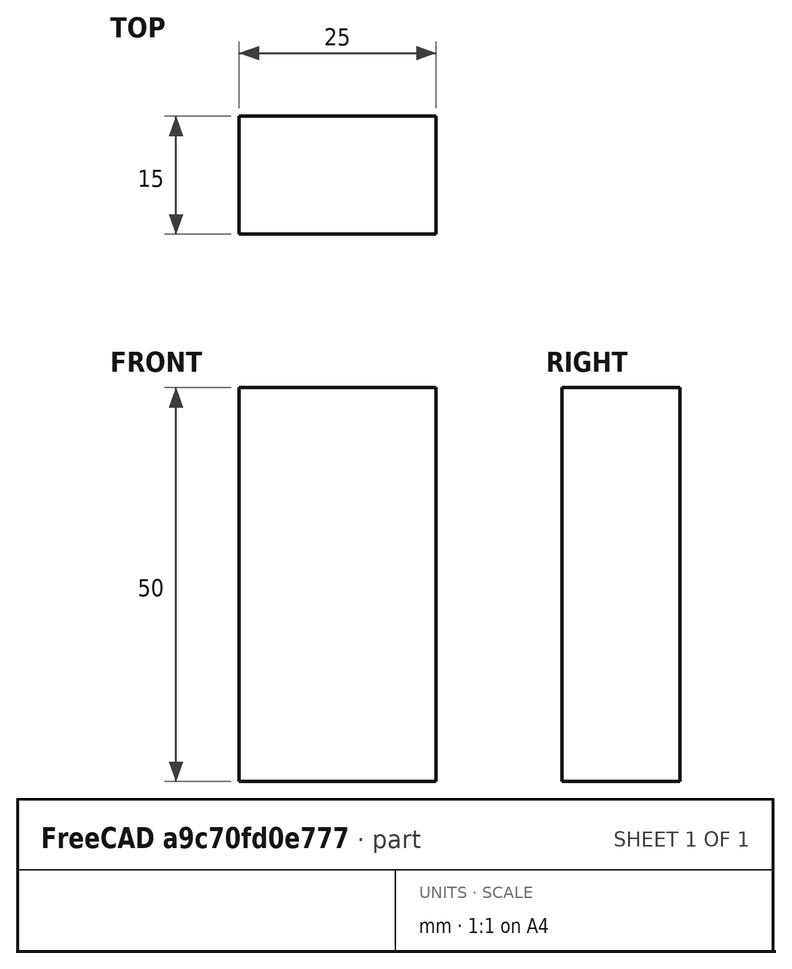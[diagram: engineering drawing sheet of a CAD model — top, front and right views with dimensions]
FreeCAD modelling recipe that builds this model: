
FCSTD DOCUMENT  (FreeCAD 0.15R4671 (Git))
Label: Flat Bar 25x15 EN10058 S235JR
License: All rights reserved
LicenseURL: http://en.wikipedia.org/wiki/All_rights_reserved
objects: Sketcher::SketchObject×1, Part::Extrusion×1
note: 2 computed .brp shape members not serialized (recipe doc carries the construction recipe); baked Part::Feature solids carry a one-line shape summary decoded from their .brp

FEATURE [Sketcher::SketchObject] Sketch
  sketch-geometry (4):
    g0: LineSegment StartX=-12.5 StartY=-7.5 StartZ=0 EndX=12.5 EndY=-7.5 EndZ=0
    g1: LineSegment StartX=12.5 StartY=-7.5 StartZ=0 EndX=12.5 EndY=7.5 EndZ=0
    g2: LineSegment StartX=12.5 StartY=7.5 StartZ=0 EndX=-12.5 EndY=7.5 EndZ=0
    g3: LineSegment StartX=-12.5 StartY=7.5 StartZ=0 EndX=-12.5 EndY=-7.5 EndZ=0
  constraints (12):
    c: Coincident(g0,g1)
    c: Coincident(g1,g2)
    c: Coincident(g2,g3)
    c: Coincident(g3,g0)
    c: Horizontal(g0)
    c: Horizontal(g2)
    c: Vertical(g1)
    c: Vertical(g3)
    c: Symmetric(g1,g2,g-2)
    c: Symmetric(g0,g1,g-1)
    c: DistanceY(g1) = 15
    c: DistanceX(g0) = 25
FEATURE [Part::Extrusion] Extrude  label="Flat Bar 25x15 EN10058 S235JR"
  Base = -> Sketch
  Dir = (0,0,50)
  Solid = true
